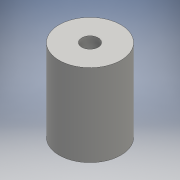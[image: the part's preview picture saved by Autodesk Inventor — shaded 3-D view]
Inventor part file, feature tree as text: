
AUTODESK INVENTOR PART (.ipt)
format: ipt  version: 2016 (Build 200138000, 138)  size: 88,576 bytes
history: native  units: mm
features: extrude x1, sketch x1
ambient origin geometry x8: Origin, YZ Plane, XZ Plane, XY Plane, X Axis, Y Axis, Z Axis, Center Point
bodies: Solid1 (feature_tree)
feature tree (2):
  extrude  "Extrusion1"  Depth=25.0mm
  sketch  "Sketch1"  dims[d0=18.75mm d1=5.0mm d2=25.0mm d3=0.0mm]
